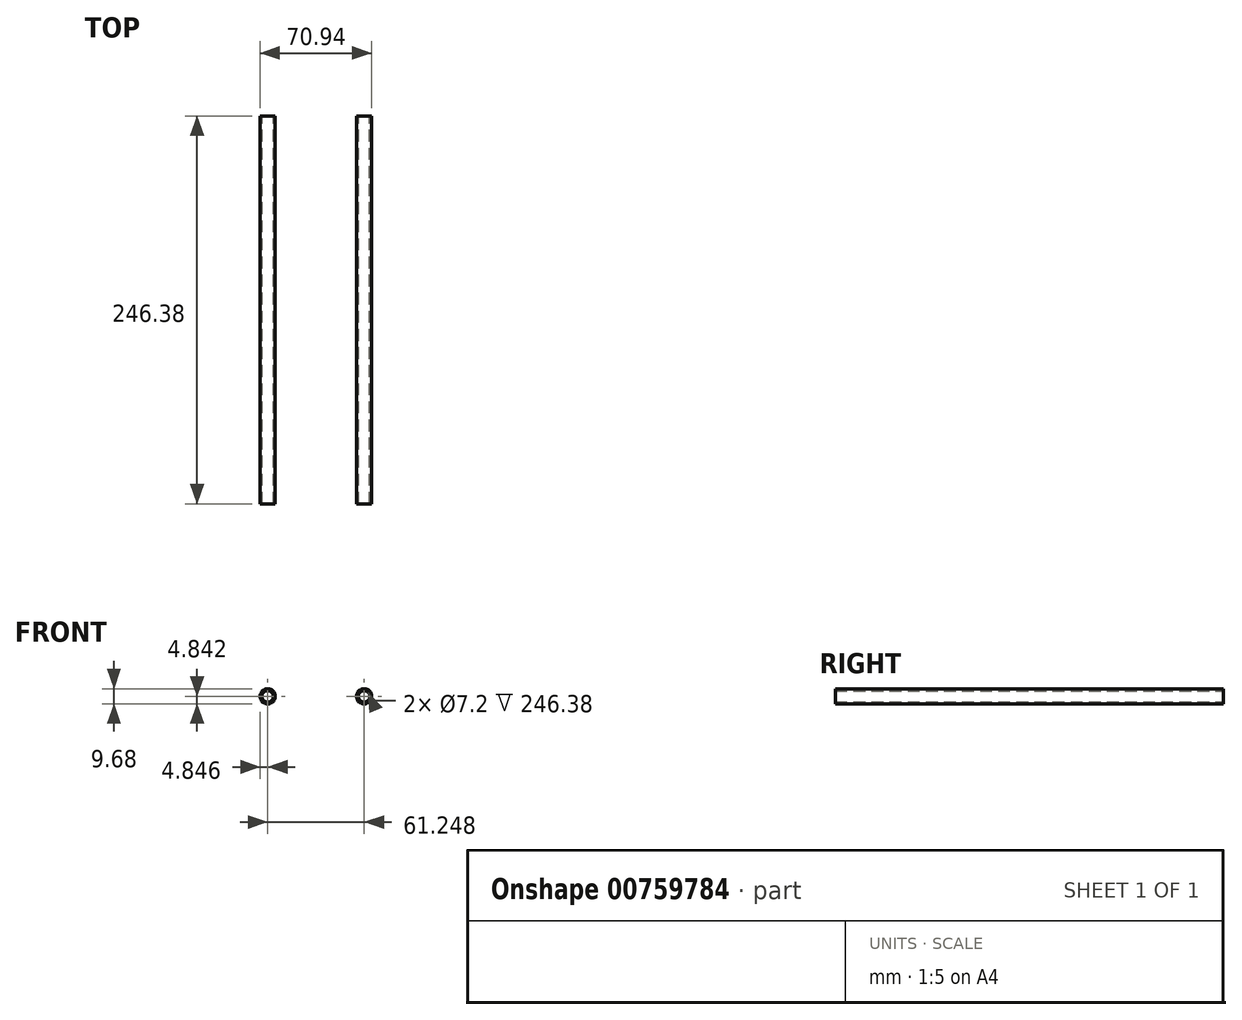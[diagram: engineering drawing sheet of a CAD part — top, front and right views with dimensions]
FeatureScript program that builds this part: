
annotation { "Feature Type Name" : "Feature", "Feature Type Description" : "" }
export const myFeature = defineFeature(function(context is Context, id is Id, definition is map)
    precondition{}
    {
        {
            var Q0;
            Q0=qCreatedBy(makeId("Front.planeOp"),FACE);
            var sketch = newSketch(context, id + "F0", { "sketchPlane" : qUnion([Q0])});
            skCircle(sketch, "E0", {"center": v(-30.62, 11.86) * mm, "radius": 4.84 * mm});
            skCircle(sketch, "E1", {"center": v(-30.62, 11.86) * mm, "radius": 3.6 * mm});
            skSolve(sketch);
        }
        {
            var Q0;
            Q0 = qSketchRegion(id + "F0", true);
            extrude(context, id + "F1", {"entities" : qUnion([Q0]), "depth" : 246.38 * mm, "offsetDistance" : 25.4 * mm});
        }
        {
            var Q0;
            Q0=makeQuery(id+"F1.opExtrude","SWEPT_BODY",BODY,{"disambiguationData":[OSD([sQuery(id+"F0.wireOp",EDGE,"E0"),sQuery(id+"F0.wireOp",EDGE,"E1")])]});
            var Q1;
            Q1=qCreatedBy(makeId("Right.planeOp"),FACE);
            mirror(context, id + "F2", {"entities" : qUnion([Q0]), "mirrorPlane" : qUnion([Q1])});
        }
    });
